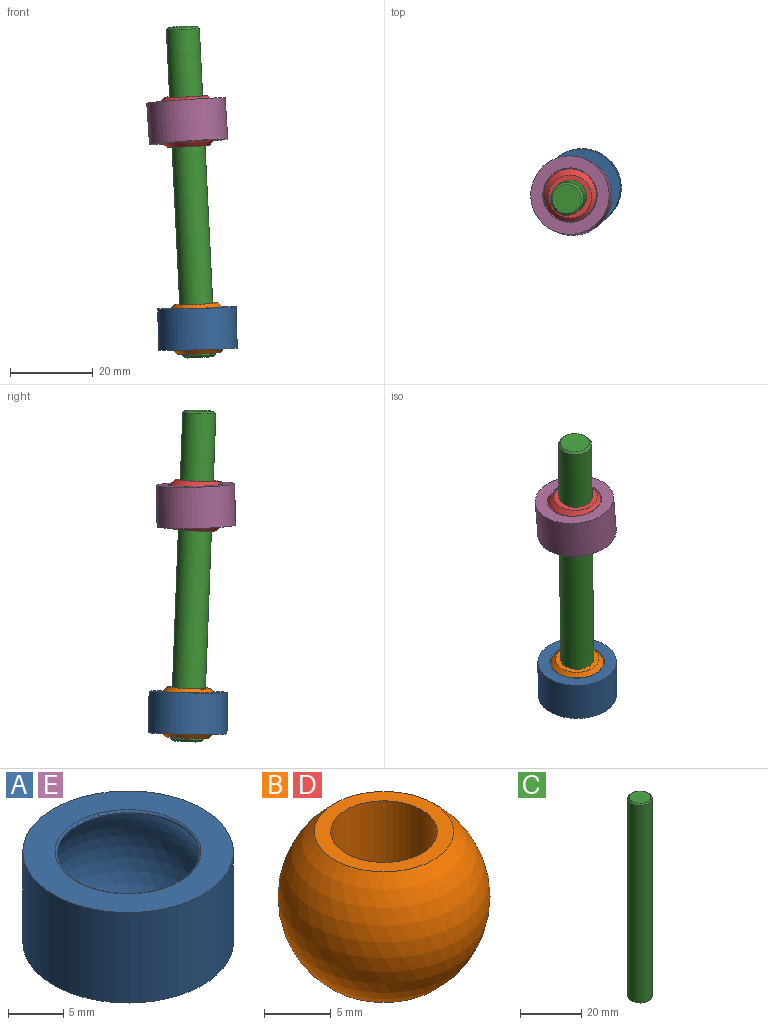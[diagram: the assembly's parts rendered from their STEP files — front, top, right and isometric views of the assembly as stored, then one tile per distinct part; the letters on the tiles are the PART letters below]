
ASSEMBLY  parts=5 mates=4
PART A: 6 faces, bbox 19x19x10 mm
  f0: plane 19x19mm, normal (0,0,1), area 147.2mm2, adj f3,f4
  f1: sphere r=7.95mm, area 467.8mm2, adj f4,f5
  f2: plane 19x19mm, normal (0,0,-1), area 147.2mm2, adj f3,f5
  f3: cylinder r=9.5mm len=19mm, axis (0,0,1), area 596.9mm2, adj f0,f2
  f4: torus R=6.59mm, axis (0,0,1), area 17.8mm2, adj f0,f1
  f5: torus R=6.59mm, axis (0,0,-1), area 17.8mm2, adj f1,f2
PART B: 4 faces, bbox 15.9x15.9x12 mm
  f0: cylinder r=4mm len=12mm, axis (0,0,1), area 301.6mm2, adj f1,f3
  f1: plane 10.43x10.43mm, normal (0,0,-1), area 35.2mm2, adj f0,f2
  f2: sphere r=7.95mm, area 599.4mm2, adj f1,f3
  f3: plane 10.43x10.43mm, normal (0,0,1), area 35.2mm2, adj f0,f2
PART C: 5 faces, bbox 8x8x80 mm
  f0: cylinder r=4mm len=79mm, axis (0,0,-1), area 1985.5mm2, adj f3,f4
  f1: plane 7x7mm, normal (0,0,1), area 38.5mm2, adj f3
  f2: plane 7x7mm, normal (0,0,-1), area 38.5mm2, adj f4
  f3: cone r=3.5mm half-angle=45deg, axis (0,0,-1), area 16.7mm2, adj f0,f1
  f4: cone r=4mm half-angle=45deg, axis (0,0,1), area 16.7mm2, adj f0,f2
PART D: same geometry as B
PART E: same geometry as A
PLACE A rot(axis=(0.49,-0.86,-0.09),1.8deg) t=(-31.78,-0.82,-5)mm
PLACE B rot(axis=(0.05,-0.01,-1),75deg) t=(-31.78,-0.82,-5)mm
PLACE C rot(axis=(0.16,-0.26,0.95),11.5deg) t=(-31.44,-0.56,-11.91)mm
PLACE D rot(axis=(0.12,-0.2,0.97),15.5deg) t=(-34.22,-2.72,45.14)mm
PLACE E rot(axis=(-0.07,-0.08,0.99),40.1deg) t=(-34.22,-2.72,45.14)mm
MATE cylindrical C.f0 <-> B.f0  axis (-0.05,-0.04,1) through (-35.33,-3.58,67.93)mm
MATE cylindrical D.f0 <-> C.f0  axis (-0.05,-0.04,1) through (-34.22,-2.72,45.14)mm
MATE ball B.f0 <-> A.f4  axis (-0.05,-0.04,1) through (-31.78,-0.82,-5)mm
MATE ball E.f4 <-> D.f0  axis (-0.07,0.02,1) through (-34.22,-2.72,45.14)mm
